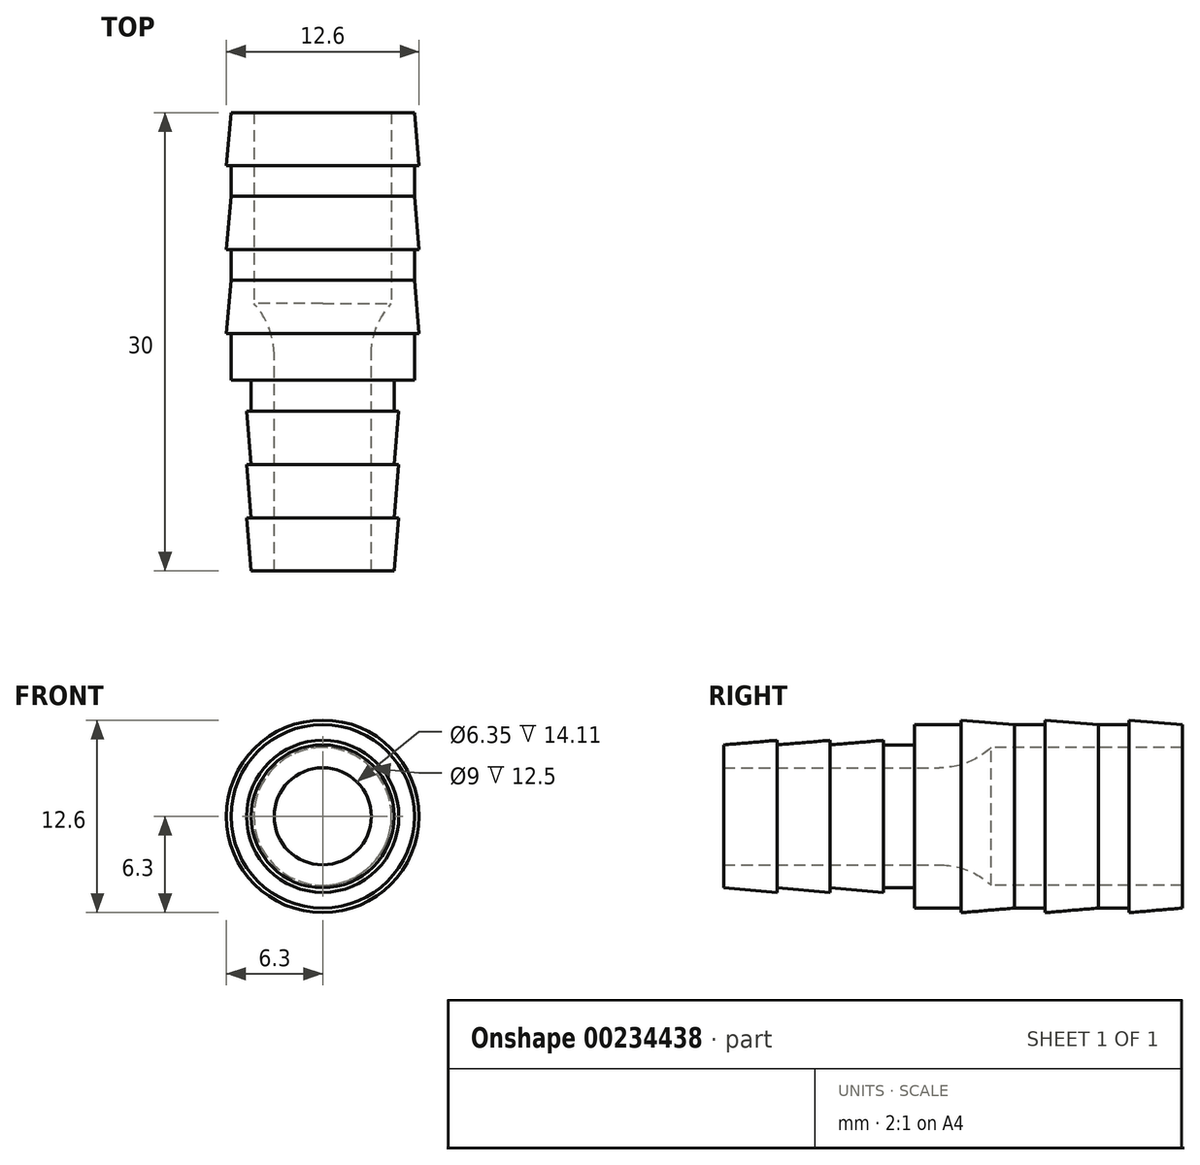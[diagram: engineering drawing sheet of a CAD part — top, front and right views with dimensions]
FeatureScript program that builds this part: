
annotation { "Feature Type Name" : "Feature", "Feature Type Description" : "" }
export const myFeature = defineFeature(function(context is Context, id is Id, definition is map)
    precondition{}
    {
        {
            var Q0;
            Q0=qCreatedBy(makeId("Front.planeOp"),FACE);
            var sketch = newSketch(context, id + "F0", { "sketchPlane" : qUnion([Q0])});
            skCircle(sketch, "E0", {"center": v(0, 0) * mm, "radius": 3.17 * mm});
            skCircle(sketch, "E1", {"center": v(0, 0) * mm, "radius": 4.68 * mm});
            skSolve(sketch);
        }
        {
            var Q0;
            Q0=qSketchRegion(id+"F0",true);
            extrude(context, id + "F1", {"entities" : qUnion([Q0]), "depth" : 15 * mm, "offsetDistance" : 25 * mm, "hasSecondDirection" : true, "secondDirectionOppositeDirection" : true, "secondDirectionDepth" : 2.5 * mm});
        }
        {
            var Q0;
            Q0=qCreatedBy(makeId("Front.planeOp"),FACE);
            var sketch = newSketch(context, id + "F2", { "sketchPlane" : qUnion([Q0])});
            skCircle(sketch, "E2", {"center": v(0, 0) * mm, "radius": 4.5 * mm});
            skCircle(sketch, "E3", {"center": v(0, 0) * mm, "radius": 6 * mm});
            skSolve(sketch);
        }
        {
            var Q0;
            Q0=qSketchRegion(id+"F2",true);
            extrude(context, id + "F3", {"entities" : qUnion([Q0]), "operationType" : NewBodyOperationType.ADD, "oppositeDirection" : true, "depth" : 15 * mm, "offsetDistance" : 25 * mm, "hasSecondDirection" : true, "secondDirectionOppositeDirection" : false, "secondDirectionDepth" : 2.5 * mm});
        }
        {
            var Q0;
            Q0=qCreatedBy(makeId("Right.planeOp"),FACE);
            var sketch = newSketch(context, id + "F4", { "sketchPlane" : qUnion([Q0])});
            skLineSegment(sketch, "E4", {"start": v(-15, 4.68) * mm, "end": v(-2.5, 4.68) * mm, "construction": true});
            skLineSegment(sketch, "E5", {"start": v(-2.5, 6) * mm, "end": v(15, 6) * mm, "construction": true});
            skLineSegment(sketch, "E6", {"start": v(-15, 4.68) * mm, "end": v(-11.51, 4.98) * mm});
            skLineSegment(sketch, "E7", {"start": v(-11.51, 4.98) * mm, "end": v(-11.51, 4.68) * mm});
            skLineSegment(sketch, "E8", {"start": v(-11.51, 4.68) * mm, "end": v(-15, 4.68) * mm});
            skLineSegment(sketch, "E9", {"start": v(0, 0) * mm, "end": v(-27.62, 0) * mm, "construction": true});
            skLineSegment(sketch, "E10", {"start": v(-11.51, 4.68) * mm, "end": v(-8.03, 4.98) * mm});
            skLineSegment(sketch, "E11", {"start": v(-8.03, 4.98) * mm, "end": v(-8.03, 4.68) * mm});
            skLineSegment(sketch, "E12", {"start": v(-11.51, 4.68) * mm, "end": v(-8.03, 4.68) * mm});
            skLineSegment(sketch, "E13", {"start": v(-8.03, 4.68) * mm, "end": v(-4.54, 4.98) * mm});
            skLineSegment(sketch, "E14", {"start": v(-4.54, 4.98) * mm, "end": v(-4.54, 4.68) * mm});
            skLineSegment(sketch, "E15", {"start": v(-4.54, 4.68) * mm, "end": v(-8.03, 4.68) * mm});
            skLineSegment(sketch, "E16", {"start": v(15, 6) * mm, "end": v(11.51, 6.3) * mm});
            skLineSegment(sketch, "E17", {"start": v(11.51, 6.3) * mm, "end": v(11.51, 6) * mm});
            skLineSegment(sketch, "E18", {"start": v(11.51, 6) * mm, "end": v(15, 6) * mm});
            skLineSegment(sketch, "E19.0", {"start": v(15, -6) * mm, "end": v(15, 6) * mm, "construction": true});
            skLineSegment(sketch, "E20", {"start": v(9.51, 6) * mm, "end": v(6.03, 6.3) * mm});
            skLineSegment(sketch, "E21", {"start": v(6.03, 6.3) * mm, "end": v(6.03, 6) * mm});
            skLineSegment(sketch, "E22", {"start": v(6.03, 6) * mm, "end": v(9.51, 6) * mm});
            skLineSegment(sketch, "E23", {"start": v(4.03, 6) * mm, "end": v(0.54, 6.3) * mm});
            skLineSegment(sketch, "E24", {"start": v(0.54, 6.3) * mm, "end": v(0.54, 6) * mm});
            skLineSegment(sketch, "E25", {"start": v(0.54, 6) * mm, "end": v(4.03, 6) * mm});
            skSolve(sketch);
        }
        {
            var Q0;
            Q0 = qSketchRegion(id + "F4", true);
            var Q1;
            Q1=sQuery(id+"F4.wireOp",EDGE,"E9");
            revolve(context, id + "F5", {"operationType" : NewBodyOperationType.ADD, "surfaceOperationType" : NewSurfaceOperationType.NEW, "entities" : qUnion([Q0]), "axis" : qUnion([Q1]), "revolveType" : RevolveType.FULL});
        }
        {
            var Q0;
            Q0=makeQuery(id+"F1.opExtrude","CAP_EDGE",EDGE,{"disambiguationData":[OSD([sQuery(id+"F0.wireOp",EDGE,"E0")])],"isStart":true});
            fillet(context, id + "F6", {"entities" : qUnion([Q0]), "radius" : 5 * mm, "tangentPropagation" : true, "allowEdgeOverflow" : false});
        }
    });
